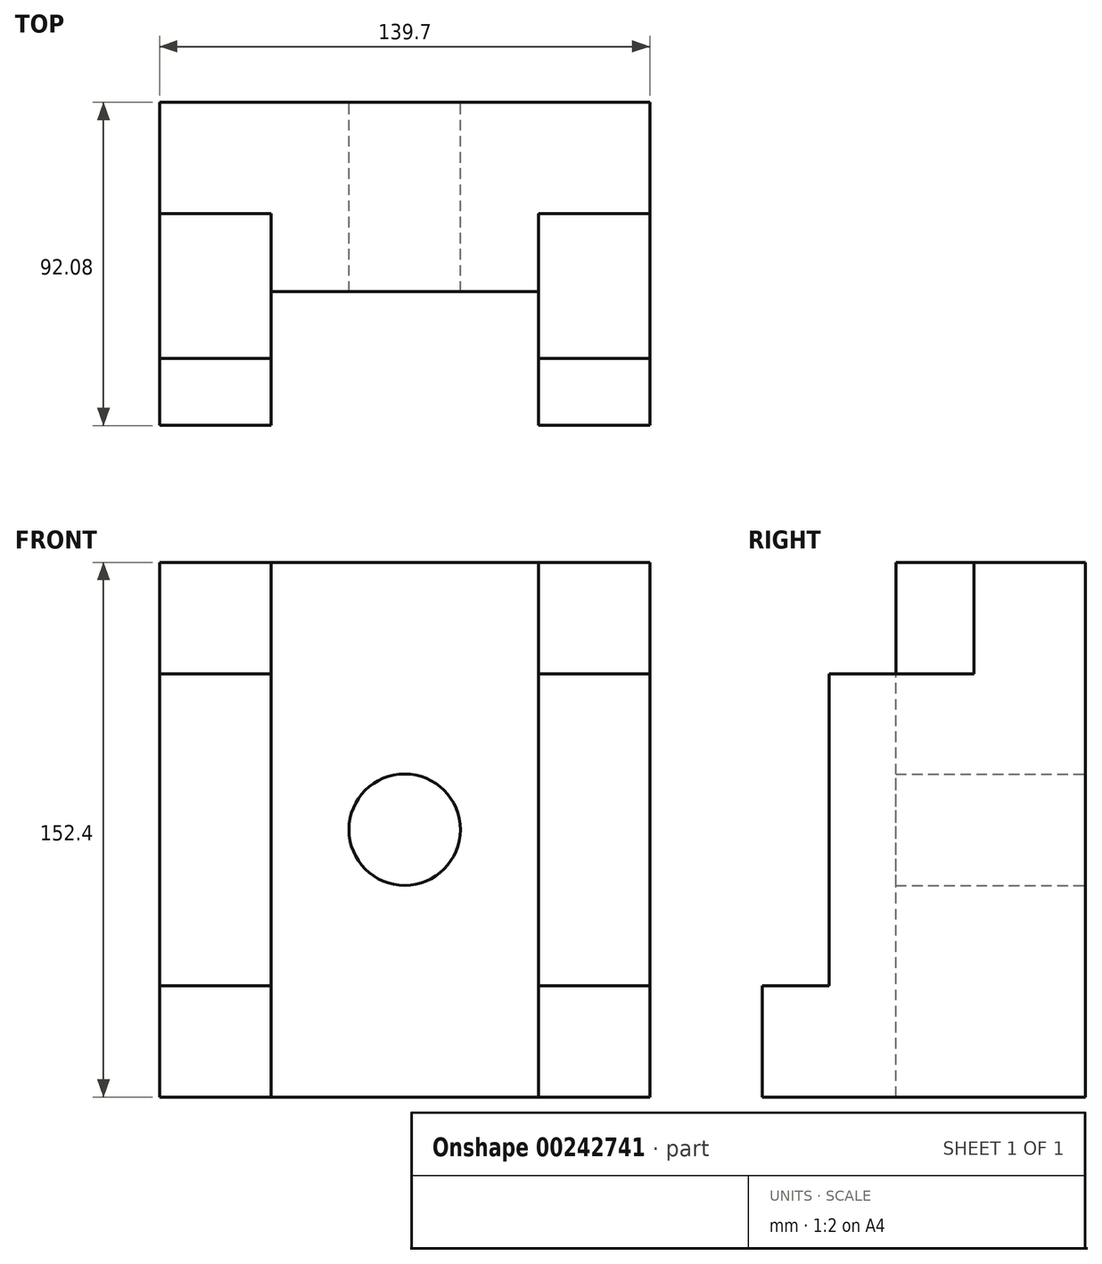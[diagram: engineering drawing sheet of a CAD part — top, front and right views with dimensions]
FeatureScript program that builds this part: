
annotation { "Feature Type Name" : "Feature", "Feature Type Description" : "" }
export const myFeature = defineFeature(function(context is Context, id is Id, definition is map)
    precondition{}
    {
        {
            var Q0;
            Q0=qCreatedBy(makeId("Front.planeOp"),FACE);
            var sketch = newSketch(context, id + "F0", { "sketchPlane" : qUnion([Q0])});
            skLineSegment(sketch, "E0.left", {"start": v(-139.35, 101.6) * mm, "end": v(-139.35, 50.8) * mm});
            skLineSegment(sketch, "E0.right", {"start": v(114.65, 101.6) * mm, "end": v(114.65, 50.8) * mm});
            skLineSegment(sketch, "E1.bottom", {"start": v(73.38, 0) * mm, "end": v(114.65, 0) * mm});
            skLineSegment(sketch, "E1.top", {"start": v(57.5, -50.8) * mm, "end": v(114.65, -50.8) * mm});
            skLineSegment(sketch, "E1.right", {"start": v(114.65, 0) * mm, "end": v(114.65, -50.8) * mm});
            skLineSegment(sketch, "E2.bottom", {"start": v(114.65, 50.8) * mm, "end": v(73.38, 50.8) * mm});
            skLineSegment(sketch, "E2.top", {"start": v(114.65, 0) * mm, "end": v(73.38, 0) * mm});
            skLineSegment(sketch, "E2.right", {"start": v(73.38, 50.8) * mm, "end": v(73.38, 0) * mm});
            skLineSegment(sketch, "E3.top", {"start": v(73.38, 50.8) * mm, "end": v(114.65, 50.8) * mm});
            skLineSegment(sketch, "E4", {"start": v(-98.07, 0) * mm, "end": v(-139.35, 0) * mm});
            skLineSegment(sketch, "E5", {"start": v(-98.07, 50.8) * mm, "end": v(-139.35, 50.8) * mm});
            skLineSegment(sketch, "E6.bottom", {"start": v(-139.35, 50.8) * mm, "end": v(-98.07, 50.8) * mm});
            skLineSegment(sketch, "E6.top", {"start": v(-139.35, 0) * mm, "end": v(-98.07, 0) * mm});
            skLineSegment(sketch, "E6.right", {"start": v(-98.07, 50.8) * mm, "end": v(-98.07, 0) * mm});
            skLineSegment(sketch, "E7", {"start": v(-12.35, 101.6) * mm, "end": v(-12.35, -50.8) * mm, "construction": true});
            skCircle(sketch, "E8", {"center": v(-12.35, 25.4) * mm, "radius": 15.88 * mm});
            skLineSegment(sketch, "E9.trimOffspring", {"start": v(-139.35, 0) * mm, "end": v(-139.35, -50.8) * mm});
            skLineSegment(sketch, "E10", {"start": v(-50.45, 69.85) * mm, "end": v(-50.45, -19.05) * mm});
            skLineSegment(sketch, "E11", {"start": v(-50.45, -50.8) * mm, "end": v(-50.45, -19.05) * mm});
            skLineSegment(sketch, "E12", {"start": v(25.75, -19.05) * mm, "end": v(25.75, -50.8) * mm});
            skLineSegment(sketch, "E13", {"start": v(25.75, -50.8) * mm, "end": v(25.75, -19.05) * mm});
            skLineSegment(sketch, "E14.bottom", {"start": v(25.75, -19.05) * mm, "end": v(57.5, -19.05) * mm});
            skLineSegment(sketch, "E14.top", {"start": v(25.75, -50.8) * mm, "end": v(57.5, -50.8) * mm});
            skLineSegment(sketch, "E14.right", {"start": v(57.5, -19.05) * mm, "end": v(57.5, -50.8) * mm});
            skLineSegment(sketch, "E15.trimOffspring", {"start": v(-50.45, -50.8) * mm, "end": v(25.75, -50.8) * mm});
            skLineSegment(sketch, "E16.bottom", {"start": v(-50.45, -19.05) * mm, "end": v(-82.2, -19.05) * mm});
            skLineSegment(sketch, "E16.left", {"start": v(-50.45, -19.05) * mm, "end": v(-50.45, -50.8) * mm});
            skLineSegment(sketch, "E17.top", {"start": v(-82.2, 69.85) * mm, "end": v(-50.45, 69.85) * mm});
            skLineSegment(sketch, "E18.top", {"start": v(25.75, 69.85) * mm, "end": v(57.5, 69.85) * mm});
            skLineSegment(sketch, "E18.left", {"start": v(25.75, 101.6) * mm, "end": v(25.75, 69.85) * mm});
            skLineSegment(sketch, "E18.right", {"start": v(57.5, 101.6) * mm, "end": v(57.5, 69.85) * mm});
            skLineSegment(sketch, "E19", {"start": v(25.75, 69.85) * mm, "end": v(25.75, -19.05) * mm});
            skLineSegment(sketch, "E20", {"start": v(57.5, 69.85) * mm, "end": v(57.5, -19.05) * mm});
            skLineSegment(sketch, "E21", {"start": v(-139.35, 101.6) * mm, "end": v(-82.2, 101.6) * mm});
            skLineSegment(sketch, "E22", {"start": v(-12.35, 101.6) * mm, "end": v(-50.45, 101.6) * mm});
            skLineSegment(sketch, "E23", {"start": v(25.75, 101.6) * mm, "end": v(-12.35, 101.6) * mm});
            skLineSegment(sketch, "E24", {"start": v(57.5, 101.6) * mm, "end": v(25.75, 101.6) * mm});
            skLineSegment(sketch, "E25", {"start": v(114.65, 101.6) * mm, "end": v(57.5, 101.6) * mm});
            skLineSegment(sketch, "E26", {"start": v(-50.45, -50.8) * mm, "end": v(-139.35, -50.8) * mm});
            skLineSegment(sketch, "E27", {"start": v(-82.2, -50.8) * mm, "end": v(-82.2, 69.85) * mm});
            skLineSegment(sketch, "E28", {"start": v(-50.45, 69.85) * mm, "end": v(-50.45, 101.6) * mm});
            skLineSegment(sketch, "E29", {"start": v(-82.2, 69.85) * mm, "end": v(-82.2, 101.6) * mm});
            skLineSegment(sketch, "E30", {"start": v(-82.2, 101.6) * mm, "end": v(-50.45, 101.6) * mm});
            skSolve(sketch);
        }
        {
            var Q0;
            Q0=makeQuery(id+"F0.imprint","IMPRINT",FACE,{"disambiguationData":[TD([[makeQuery(id+"F0.imprint","IMPRINT",EDGE,{"derivedFrom":sQuery(id+"F0.wireOp",EDGE,"E2.top")}),1.0]])]});
            var Q1;
            Q1=makeQuery(id+"F0.imprint","IMPRINT",FACE,{"disambiguationData":[TD([[makeQuery(id+"F0.imprint","IMPRINT",EDGE,{"derivedFrom":sQuery(id+"F0.wireOp",EDGE,"E18.bottom")}),-1.0]])]});
            var Q2;
            Q2=makeQuery(id+"F0.imprint","IMPRINT",FACE,{"disambiguationData":[TD([[makeQuery(id+"F0.imprint","IMPRINT",EDGE,{"derivedFrom":sQuery(id+"F0.wireOp",EDGE,"E14.bottom")}),1.0]])]});
            var Q3;
            Q3=makeQuery(id+"F0.imprint","IMPRINT",FACE,{"disambiguationData":[TD([[makeQuery(id+"F0.imprint","IMPRINT",EDGE,{"derivedFrom":sQuery(id+"F0.wireOp",EDGE,"E14.bottom")}),-1.0]])]});
            var Q4;
            Q4=makeQuery(id+"F0.imprint","IMPRINT",FACE,{"disambiguationData":[TD([[makeQuery(id+"F0.imprint","IMPRINT",EDGE,{"derivedFrom":sQuery(id+"F0.wireOp",EDGE,"E8")}),-1.0]])]});
            var Q5;
            Q5=makeQuery(id+"F0.imprint","IMPRINT",FACE,{"disambiguationData":[TD([[makeQuery(id+"F0.imprint","IMPRINT",EDGE,{"derivedFrom":sQuery(id+"F0.wireOp",EDGE,"E10")}),-1.0]])]});
            var Q6;
            Q6=makeQuery(id+"F0.imprint","IMPRINT",FACE,{"disambiguationData":[TD([[makeQuery(id+"F0.imprint","IMPRINT",EDGE,{"derivedFrom":sQuery(id+"F0.wireOp",EDGE,"E16.bottom")}),1.0]])]});
            var Q7;
            Q7=makeQuery(id+"F0.imprint","IMPRINT",FACE,{"disambiguationData":[TD([[makeQuery(id+"F0.imprint","IMPRINT",EDGE,{"derivedFrom":sQuery(id+"F0.wireOp",EDGE,"E17.bottom")}),-1.0]])]});
            var Q8;
            Q8=makeQuery(id+"F0.imprint","IMPRINT",FACE,{"disambiguationData":[TD([[makeQuery(id+"F0.imprint","IMPRINT",EDGE,{"derivedFrom":sQuery(id+"F0.wireOp",EDGE,"E0.bottom")}),-1.0]])]});
            var Q9;
            Q9=makeQuery(id+"F0.imprint","IMPRINT",FACE,{"disambiguationData":[TD([[makeQuery(id+"F0.imprint","IMPRINT",EDGE,{"derivedFrom":sQuery(id+"F0.wireOp",EDGE,"E0.top")}),1.0]])]});
            var Q10;
            Q10=makeQuery(id+"F0.imprint","IMPRINT",FACE,{"disambiguationData":[TD([[makeQuery(id+"F0.imprint","IMPRINT",EDGE,{"derivedFrom":sQuery(id+"F0.wireOp",EDGE,"E17.top")}),1.0]])]});
            var Q11;
            Q11=makeQuery(id+"F0.imprint","IMPRINT",FACE,{"disambiguationData":[TD([[makeQuery(id+"F0.imprint","IMPRINT",EDGE,{"derivedFrom":sQuery(id+"F0.wireOp",EDGE,"E18.top")}),1.0]])]});
            extrude(context, id + "F1", {"entities" : qUnion([Q0, Q1, Q2, Q3, Q4, Q5, Q6, Q7, Q8, Q9, Q10, Q11]), "depth" : 31.75 * mm});
        }
        {
            var Q0;
            Q0=makeQuery(id+"F0.imprint","IMPRINT",FACE,{"disambiguationData":[TD([[makeQuery(id+"F0.imprint","IMPRINT",EDGE,{"derivedFrom":sQuery(id+"F0.wireOp",EDGE,"E17.bottom")}),-1.0]])]});
            var Q1;
            Q1=makeQuery(id+"F0.imprint","IMPRINT",FACE,{"disambiguationData":[TD([[makeQuery(id+"F0.imprint","IMPRINT",EDGE,{"derivedFrom":sQuery(id+"F0.wireOp",EDGE,"E10")}),-1.0]])]});
            var Q2;
            Q2=makeQuery(id+"F0.imprint","IMPRINT",FACE,{"disambiguationData":[TD([[makeQuery(id+"F0.imprint","IMPRINT",EDGE,{"derivedFrom":sQuery(id+"F0.wireOp",EDGE,"E16.bottom")}),1.0]])]});
            extrude(context, id + "F2", {"entities" : qUnion([Q0, Q1, Q2]), "operationType" : NewBodyOperationType.ADD, "depth" : 73.02 * mm});
        }
        {
            var Q0;
            Q0=makeQuery(id+"F0.imprint","IMPRINT",FACE,{"disambiguationData":[TD([[makeQuery(id+"F0.imprint","IMPRINT",EDGE,{"derivedFrom":sQuery(id+"F0.wireOp",EDGE,"E14.bottom")}),-1.0]])]});
            var Q1;
            Q1=makeQuery(id+"F0.imprint","IMPRINT",FACE,{"disambiguationData":[TD([[makeQuery(id+"F0.imprint","IMPRINT",EDGE,{"derivedFrom":sQuery(id+"F0.wireOp",EDGE,"E14.bottom")}),1.0]])]});
            var Q2;
            Q2=makeQuery(id+"F0.imprint","IMPRINT",FACE,{"disambiguationData":[TD([[makeQuery(id+"F0.imprint","IMPRINT",EDGE,{"derivedFrom":sQuery(id+"F0.wireOp",EDGE,"E18.bottom")}),-1.0]])]});
            extrude(context, id + "F3", {"entities" : qUnion([Q0, Q1, Q2]), "operationType" : NewBodyOperationType.ADD, "depth" : 73.02 * mm});
        }
        {
            var Q0;
            Q0=makeQuery(id+"F0.imprint","IMPRINT",FACE,{"disambiguationData":[TD([[makeQuery(id+"F0.imprint","IMPRINT",EDGE,{"derivedFrom":sQuery(id+"F0.wireOp",EDGE,"E17.bottom")}),-1.0]])]});
            var Q1;
            Q1=makeQuery(id+"F0.imprint","IMPRINT",FACE,{"disambiguationData":[TD([[makeQuery(id+"F0.imprint","IMPRINT",EDGE,{"derivedFrom":sQuery(id+"F0.wireOp",EDGE,"E16.bottom")}),1.0]])]});
            var Q2;
            Q2=makeQuery(id+"F0.imprint","IMPRINT",FACE,{"disambiguationData":[TD([[makeQuery(id+"F0.imprint","IMPRINT",EDGE,{"derivedFrom":sQuery(id+"F0.wireOp",EDGE,"E18.bottom")}),-1.0]])]});
            var Q3;
            Q3=makeQuery(id+"F0.imprint","IMPRINT",FACE,{"disambiguationData":[TD([[makeQuery(id+"F0.imprint","IMPRINT",EDGE,{"derivedFrom":sQuery(id+"F0.wireOp",EDGE,"E14.bottom")}),-1.0]])]});
            extrude(context, id + "F4", {"entities" : qUnion([Q0, Q1, Q2, Q3]), "operationType" : NewBodyOperationType.ADD, "depth" : 92.07 * mm});
        }
        {
            var Q0;
            Q0=makeQuery(id+"F0.imprint","IMPRINT",FACE,{"disambiguationData":[TD([[makeQuery(id+"F0.imprint","IMPRINT",EDGE,{"derivedFrom":sQuery(id+"F0.wireOp",EDGE,"E8")}),-1.0]])]});
            extrude(context, id + "F5", {"entities" : qUnion([Q0]), "operationType" : NewBodyOperationType.ADD, "depth" : 53.97 * mm});
        }
    });
